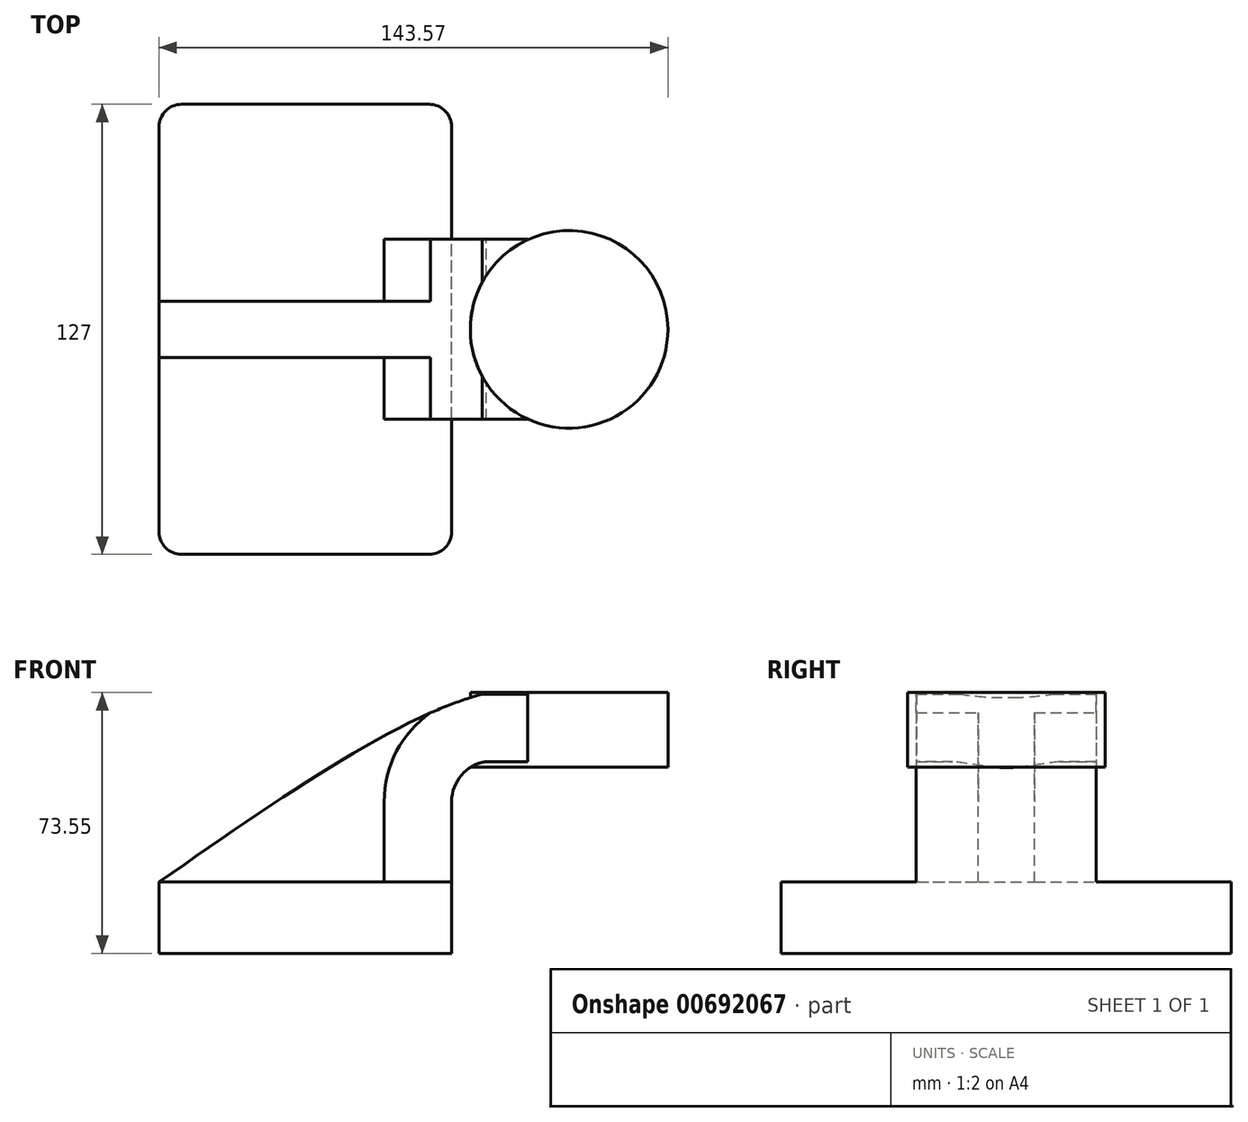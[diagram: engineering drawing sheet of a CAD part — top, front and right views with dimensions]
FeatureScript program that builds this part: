
annotation { "Feature Type Name" : "Feature", "Feature Type Description" : "" }
export const myFeature = defineFeature(function(context is Context, id is Id, definition is map)
    precondition{}
    {
        {
            var Q0;
            Q0=qCreatedBy(makeId("Front.planeOp"),FACE);
            var sketch = newSketch(context, id + "F0", { "sketchPlane" : qUnion([Q0])});
            skLineSegment(sketch, "E0.bottom", {"start": v(41.28, 10.05) * mm, "end": v(-41.28, 10.05) * mm});
            skLineSegment(sketch, "E0.top", {"start": v(41.28, -10.05) * mm, "end": v(-41.28, -10.05) * mm});
            skLineSegment(sketch, "E0.left", {"start": v(41.28, 10.05) * mm, "end": v(41.28, -10.05) * mm});
            skLineSegment(sketch, "E0.right", {"start": v(-41.28, 10.05) * mm, "end": v(-41.28, -10.05) * mm});
            skPoint(sketch, "E0.middle", {"position": v(0, 0) * mm});
            skLineSegment(sketch, "E1.bottom", {"start": v(113.52, 66.15) * mm, "end": v(62.72, 66.15) * mm});
            skLineSegment(sketch, "E1.top", {"start": v(113.52, 37.58) * mm, "end": v(62.72, 37.58) * mm});
            skLineSegment(sketch, "E1.left", {"start": v(113.52, 66.15) * mm, "end": v(113.52, 37.58) * mm});
            skLineSegment(sketch, "E1.right", {"start": v(62.72, 66.15) * mm, "end": v(62.72, 37.58) * mm});
            skPoint(sketch, "E1.middle", {"position": v(88.12, 51.86) * mm});
            skLineSegment(sketch, "E2", {"start": v(41.28, 10.05) * mm, "end": v(41.28, 32.75) * mm});
            skArc(sketch, "E3", {"start": v(51.02, 44.05) * mm, "mid": v(44.05, 40.2) * mm, "end": v(41.28, 32.75) * mm});
            skLineSegment(sketch, "E4", {"start": v(51.02, 44.05) * mm, "end": v(88.12, 44.05) * mm});
            skLineSegment(sketch, "E5.0", {"start": v(49.94, 63.1) * mm, "end": v(89.44, 63.1) * mm});
            skArc(sketch, "E5.1", {"start": v(49.94, 63.1) * mm, "mid": v(30.2, 53.3) * mm, "end": v(22.23, 32.75) * mm});
            skLineSegment(sketch, "E5.2", {"start": v(22.23, 10.05) * mm, "end": v(22.23, 32.75) * mm});
            skFitSpline(sketch, "E6", {"points": [v(-41.28, 10.05) * mm, v(49.94, 63.1) * mm, v(89.44, 63.1) * mm], "startDerivative": vector(160.35, 112.04) * mm, "endDerivative": vector(95.9, -16.23) * mm});
            skLineSegment(sketch, "E7", {"start": v(88.2, 81.56) * mm, "end": v(88.2, 23.38) * mm, "construction": true});
            skSolve(sketch);
        }
        {
            var Q0;
            Q0=makeQuery(id+"F0.imprint","IMPRINT",FACE,{"disambiguationData":[TD([[makeQuery(id+"F0.imprint","IMPRINT",EDGE,{"derivedFrom":sQuery(id+"F0.wireOp",EDGE,"E0.top")}),-1.0]])]});
            extrude(context, id + "F1", {"entities" : qUnion([Q0]), "endBound" : BoundingType.SYMMETRIC, "depth" : 127 * mm, "offsetDistance" : 25.4 * mm});
        }
        {
            var Q0;
            {var subQ1=sQuery(id+"F0.wireOp",EDGE,"E2");Q0=makeQuery(id+"F0.imprint","IMPRINT",FACE,{"disambiguationData":[TD([[makeQuery(id+"F0.imprint","IMPRINT",EDGE,{"derivedFrom":subQ1}),1.0]])]});}
            extrude(context, id + "F2", {"entities" : qUnion([Q0]), "operationType" : NewBodyOperationType.ADD, "endBound" : BoundingType.SYMMETRIC, "depth" : 50.8 * mm, "offsetDistance" : 25.4 * mm});
        }
        {
            var Q0;
            {var subQ3=sQuery(id+"F0.wireOp",EDGE,"E5.2");Q0=makeQuery(id+"F0.imprint","IMPRINT",FACE,{"disambiguationData":[TD([[makeQuery(id+"F0.imprint","IMPRINT",EDGE,{"derivedFrom":subQ3}),1.0]])]});}
            extrude(context, id + "F3", {"entities" : qUnion([Q0]), "operationType" : NewBodyOperationType.ADD, "endBound" : BoundingType.SYMMETRIC, "depth" : 15.88 * mm, "offsetDistance" : 25.4 * mm});
        }
        {
            var Q0;
            Q0=qCreatedBy(makeId("Top.planeOp"),FACE);
            var sketch = newSketch(context, id + "F4", { "sketchPlane" : qUnion([Q0])});
            skCircle(sketch, "E8", {"center": v(74.42, 0) * mm, "radius": 27.87 * mm});
            skSolve(sketch);
        }
        {
            var Q0;
            Q0 = qSketchRegion(id + "F4", true);
            extrude(context, id + "F5", {"entities" : qUnion([Q0]), "operationType" : NewBodyOperationType.ADD, "depth" : 63.5 * mm, "offsetDistance" : 25.4 * mm});
        }
        {
            var Q0;
            Q0=makeQuery(id+"F5.opExtrude","CAP_FACE",FACE,{"disambiguationData":[OSD([sQuery(id+"F4.wireOp",EDGE,"E8")])],"isStart":true});
            extrude(context, id + "F6", {"entities" : qUnion([Q0]), "operationType" : NewBodyOperationType.REMOVE, "oppositeDirection" : true, "depth" : 42.42 * mm, "offsetDistance" : 25.4 * mm});
        }
        {
            var Q0;
            Q0=makeQuery(id+"F1.opExtrude","CAP_EDGE",EDGE,{"disambiguationData":[OSD([sQuery(id+"F0.wireOp",EDGE,"E0.right")])],"isStart":false});
            var Q1;
            Q1=makeQuery(id+"F1.opExtrude","CAP_EDGE",EDGE,{"disambiguationData":[OSD([sQuery(id+"F0.wireOp",EDGE,"E0.right")])],"isStart":true});
            var Q2;
            Q2=makeQuery(id+"F1.opExtrude","CAP_EDGE",EDGE,{"disambiguationData":[OSD([sQuery(id+"F0.wireOp",EDGE,"E0.left")])],"isStart":false});
            var Q3;
            Q3=makeQuery(id+"F1.opExtrude","CAP_EDGE",EDGE,{"disambiguationData":[OSD([sQuery(id+"F0.wireOp",EDGE,"E0.left")])],"isStart":true});
            fillet(context, id + "F7", {"entities" : qUnion([Q0, Q1, Q2, Q3]), "radius" : 6.35 * mm, "tangentPropagation" : true, "allowEdgeOverflow" : false});
        }
    });
